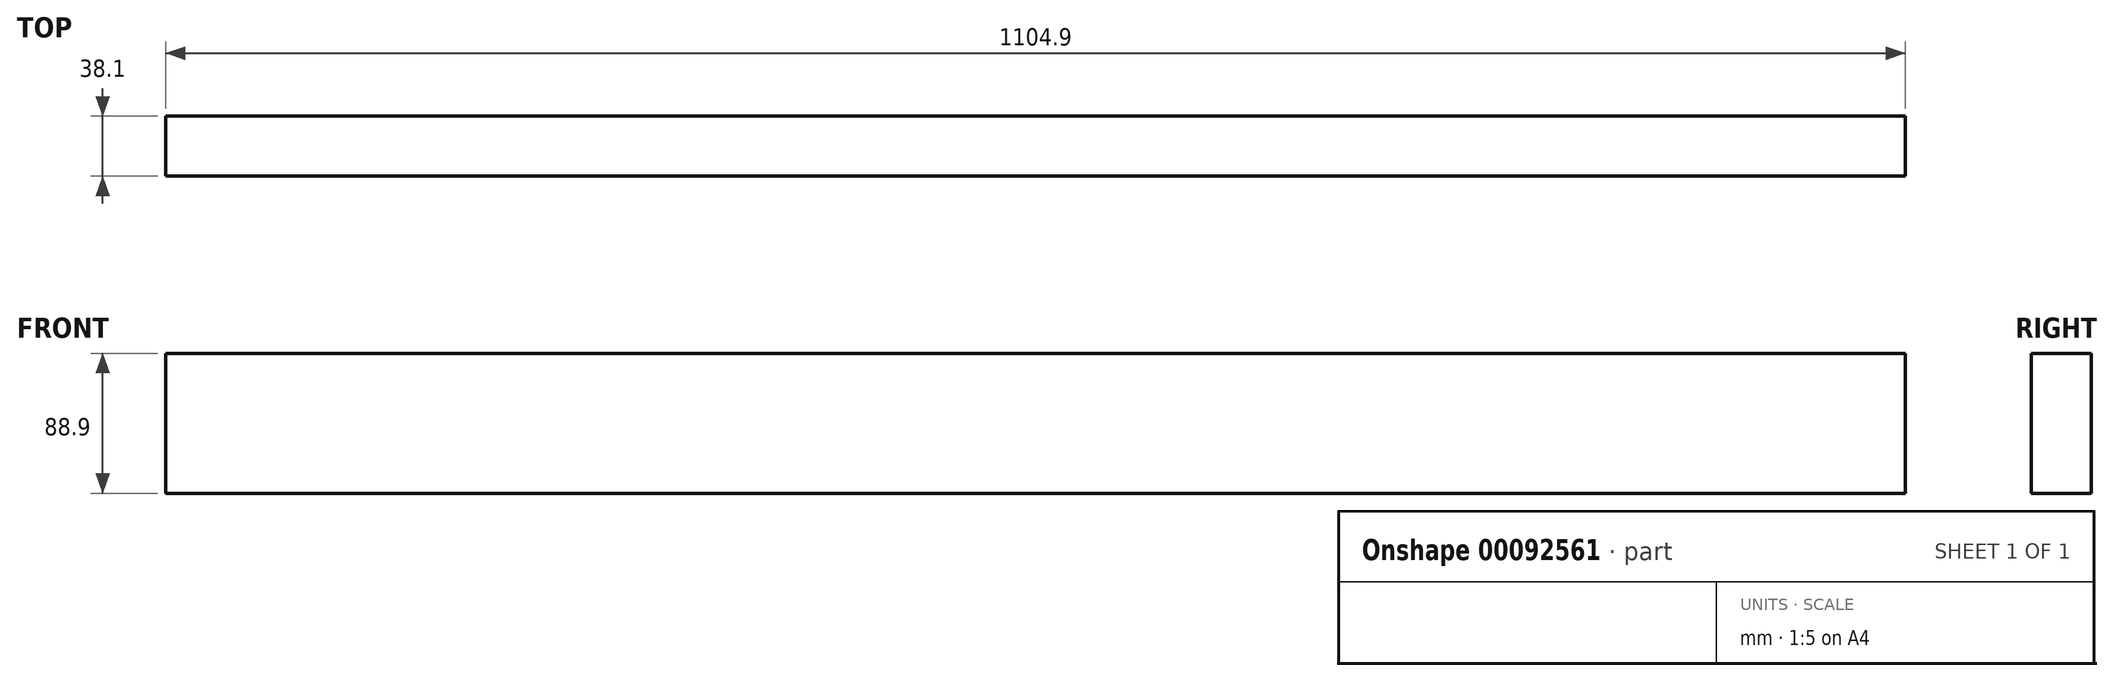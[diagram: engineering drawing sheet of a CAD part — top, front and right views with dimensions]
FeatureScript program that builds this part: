
annotation { "Feature Type Name" : "Feature", "Feature Type Description" : "" }
export const myFeature = defineFeature(function(context is Context, id is Id, definition is map)
    precondition{}
    {
        {
            var Q0;
            Q0=qCreatedBy(makeId("Front.planeOp"),FACE);
            var sketch = newSketch(context, id + "F0", { "sketchPlane" : qUnion([Q0])});
            skLineSegment(sketch, "E0.bottom", {"start": v(0, 0) * mm, "end": v(1104.9, 0) * mm});
            skLineSegment(sketch, "E0.top", {"start": v(0, 88.9) * mm, "end": v(1104.9, 88.9) * mm});
            skLineSegment(sketch, "E0.left", {"start": v(0, 0) * mm, "end": v(0, 88.9) * mm});
            skLineSegment(sketch, "E0.right", {"start": v(1104.9, 0) * mm, "end": v(1104.9, 88.9) * mm});
            skSolve(sketch);
        }
        {
            var Q0;
            Q0=makeQuery(id+"F0.imprint","IMPRINT",FACE,{"disambiguationData":[TD([[makeQuery(id+"F0.imprint","IMPRINT",EDGE,{"derivedFrom":sQuery(id+"F0.wireOp",EDGE,"E0.bottom")}),1.0]])]});
            extrude(context, id + "F1", {"entities" : qUnion([Q0]), "endBound" : BoundingType.SYMMETRIC, "depth" : 38.1 * mm});
        }
    });
